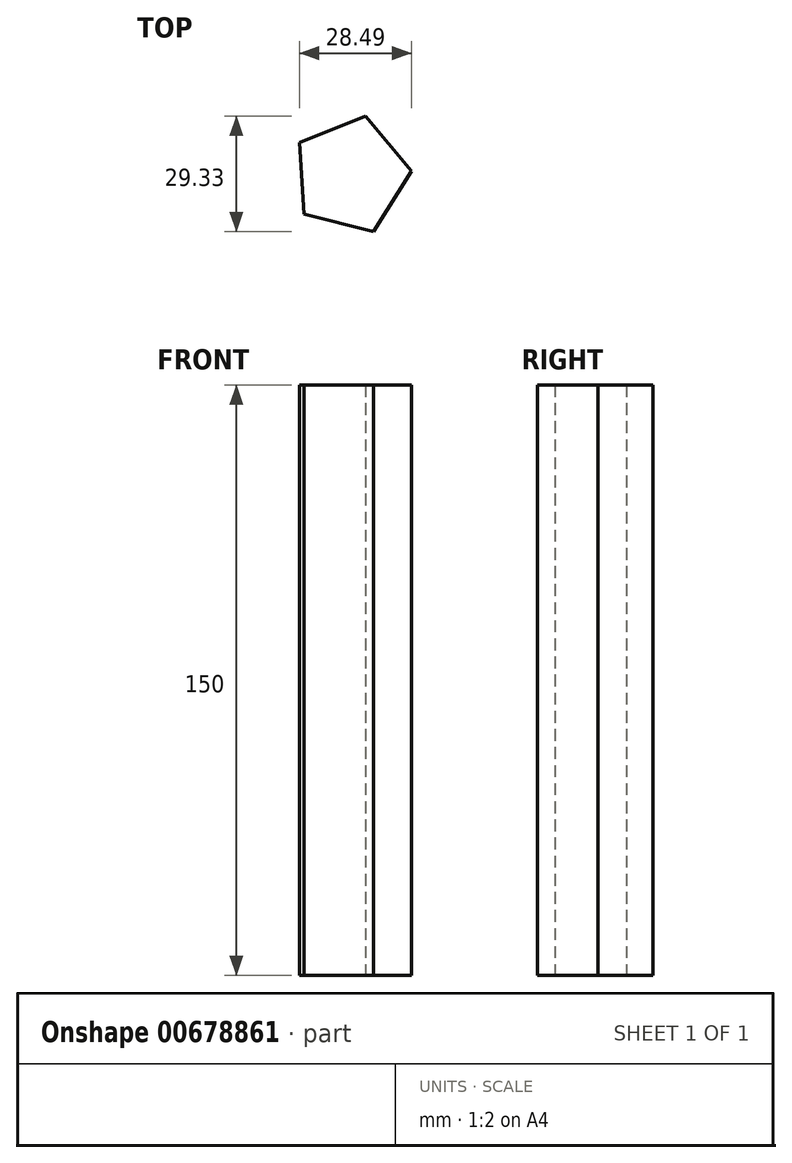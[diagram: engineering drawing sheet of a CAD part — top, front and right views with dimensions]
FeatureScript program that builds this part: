
annotation { "Feature Type Name" : "Feature", "Feature Type Description" : "" }
export const myFeature = defineFeature(function(context is Context, id is Id, definition is map)
    precondition{}
    {
        {
            var Q0;
            Q0=qCreatedBy(makeId("Top.planeOp"),FACE);
            var sketch = newSketch(context, id + "F0", { "sketchPlane" : qUnion([Q0])});
            skLineSegment(sketch, "E0.0", {"start": v(2.63, 11.48) * mm, "end": v(14.25, -2.48) * mm});
            skLineSegment(sketch, "E0.1", {"start": v(14.25, -2.48) * mm, "end": v(4.56, -17.85) * mm});
            skLineSegment(sketch, "E0.2", {"start": v(4.56, -17.85) * mm, "end": v(-13.05, -13.39) * mm});
            skLineSegment(sketch, "E0.3", {"start": v(-13.05, -13.39) * mm, "end": v(-14.24, 4.74) * mm});
            skLineSegment(sketch, "E0.4", {"start": v(-14.24, 4.74) * mm, "end": v(2.63, 11.48) * mm});
            skSolve(sketch);
        }
        {
            var Q0;
            Q0=makeQuery(id+"F0.imprint","IMPRINT",FACE,{"disambiguationData":[TD([[makeQuery(id+"F0.imprint","IMPRINT",EDGE,{"derivedFrom":sQuery(id+"F0.wireOp",EDGE,"E0.0")}),-1.0]])]});
            var Q1;
            Q1=sQuery(id+"FIAGVctAvDIoumU.wireOp",EDGE,"2d9964be-070d-4756-9806-facb3aff7fa9.0");
            var Q2;
            Q2=sQuery(id+"FIAGVctAvDIoumU.wireOp",EDGE,"2d9964be-070d-4756-9806-facb3aff7fa9.1");
            var Q3;
            Q3=sQuery(id+"FIAGVctAvDIoumU.wireOp",EDGE,"2d9964be-070d-4756-9806-facb3aff7fa9.2");
            var Q4;
            Q4=sQuery(id+"FIAGVctAvDIoumU.wireOp",EDGE,"2d9964be-070d-4756-9806-facb3aff7fa9.3");
            var Q5;
            Q5=sQuery(id+"FIAGVctAvDIoumU.wireOp",EDGE,"2d9964be-070d-4756-9806-facb3aff7fa9.4");
            var Q6;
            Q6=sQuery(id+"FIAGVctAvDIoumU.wireOp",EDGE,"2d9964be-070d-4756-9806-facb3aff7fa9.5");
            extrude(context, id + "F1", {"entities" : qUnion([Q0]), "surfaceEntities" : qUnion([Q1, Q2, Q3, Q4, Q5, Q6]), "depth" : 150 * mm, "offsetDistance" : 25 * mm});
        }
    });
